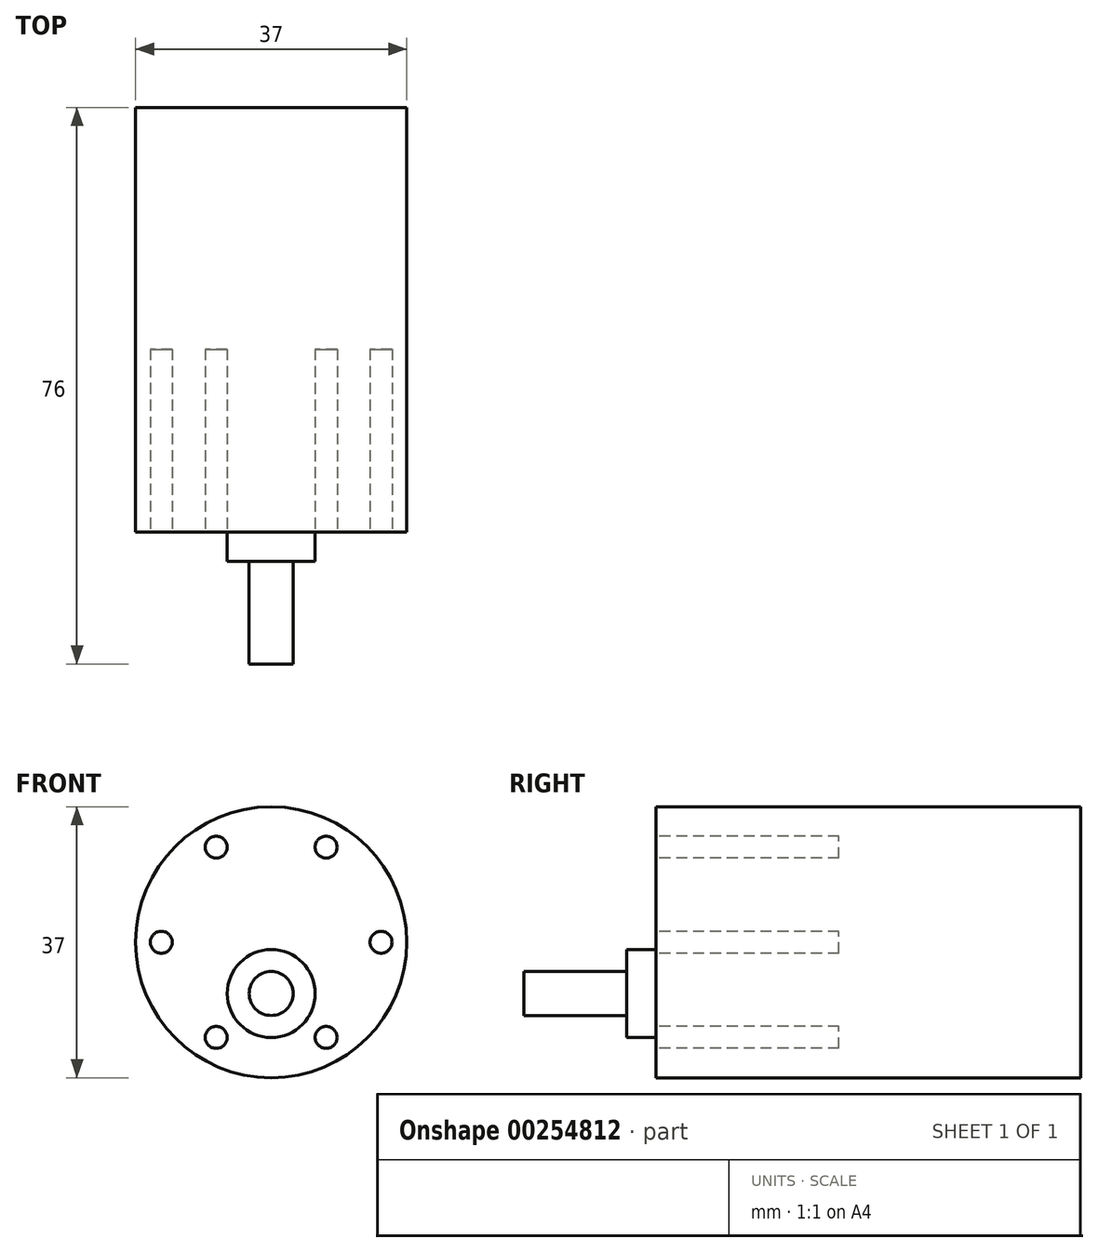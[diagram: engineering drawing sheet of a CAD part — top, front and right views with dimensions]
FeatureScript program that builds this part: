
annotation { "Feature Type Name" : "Feature", "Feature Type Description" : "" }
export const myFeature = defineFeature(function(context is Context, id is Id, definition is map)
    precondition{}
    {
        {
            var Q0;
            Q0=qCreatedBy(makeId("Front.planeOp"),FACE);
            var sketch = newSketch(context, id + "F0", { "sketchPlane" : qUnion([Q0])});
            skCircle(sketch, "E0", {"center": v(0, 0) * mm, "radius": 18.5 * mm});
            skCircle(sketch, "E1", {"center": v(0, -7) * mm, "radius": 6 * mm});
            skCircle(sketch, "E2", {"center": v(0, -7) * mm, "radius": 3 * mm});
            skCircle(sketch, "E3", {"center": v(-15, 0) * mm, "radius": 1.5 * mm});
            skCircle(sketch, "E4.1.0", {"center": v(-7.5, -13) * mm, "radius": 1.5 * mm});
            skCircle(sketch, "E4.2.0", {"center": v(7.5, -13) * mm, "radius": 1.5 * mm});
            skCircle(sketch, "E4.3.0", {"center": v(15, 0) * mm, "radius": 1.5 * mm});
            skCircle(sketch, "E4.4.0", {"center": v(7.5, 13) * mm, "radius": 1.5 * mm});
            skCircle(sketch, "E4.5.0", {"center": v(-7.5, 13) * mm, "radius": 1.5 * mm});
            skSolve(sketch);
        }
        {
            var Q0;
            Q0 = qSketchRegion(id + "F0", true);
            var Q1;
            Q1=makeQuery(id+"F0.imprint","IMPRINT",FACE,{"disambiguationData":[TD([[makeQuery(id+"F0.imprint","IMPRINT",EDGE,{"derivedFrom":sQuery(id+"F0.wireOp",EDGE,"E1")}),1.0]])]});
            var Q2;
            Q2=makeQuery(id+"F0.imprint","IMPRINT",FACE,{"disambiguationData":[TD([[makeQuery(id+"F0.imprint","IMPRINT",EDGE,{"derivedFrom":sQuery(id+"F0.wireOp",EDGE,"E2")}),1.0]])]});
            var Q3;
            Q3=makeQuery(id+"F0.imprint","IMPRINT",FACE,{"disambiguationData":[TD([[makeQuery(id+"F0.imprint","IMPRINT",EDGE,{"derivedFrom":sQuery(id+"F0.wireOp",EDGE,"E4.5.0")}),1.0]])]});
            var Q4;
            Q4=makeQuery(id+"F0.imprint","IMPRINT",FACE,{"disambiguationData":[TD([[makeQuery(id+"F0.imprint","IMPRINT",EDGE,{"derivedFrom":sQuery(id+"F0.wireOp",EDGE,"E4.4.0")}),1.0]])]});
            var Q5;
            Q5=makeQuery(id+"F0.imprint","IMPRINT",FACE,{"disambiguationData":[TD([[makeQuery(id+"F0.imprint","IMPRINT",EDGE,{"derivedFrom":sQuery(id+"F0.wireOp",EDGE,"E4.3.0")}),1.0]])]});
            var Q6;
            Q6=makeQuery(id+"F0.imprint","IMPRINT",FACE,{"disambiguationData":[TD([[makeQuery(id+"F0.imprint","IMPRINT",EDGE,{"derivedFrom":sQuery(id+"F0.wireOp",EDGE,"E4.2.0")}),1.0]])]});
            var Q7;
            Q7=makeQuery(id+"F0.imprint","IMPRINT",FACE,{"disambiguationData":[TD([[makeQuery(id+"F0.imprint","IMPRINT",EDGE,{"derivedFrom":sQuery(id+"F0.wireOp",EDGE,"E4.1.0")}),1.0]])]});
            var Q8;
            Q8=makeQuery(id+"F0.imprint","IMPRINT",FACE,{"disambiguationData":[TD([[makeQuery(id+"F0.imprint","IMPRINT",EDGE,{"derivedFrom":sQuery(id+"F0.wireOp",EDGE,"E3")}),1.0]])]});
            extrude(context, id + "F1", {"entities" : qUnion([Q0, Q1, Q2, Q3, Q4, Q5, Q6, Q7, Q8]), "oppositeDirection" : true, "depth" : 58 * mm});
        }
        {
            var Q0;
            Q0=makeQuery(id+"F0.imprint","IMPRINT",FACE,{"disambiguationData":[TD([[makeQuery(id+"F0.imprint","IMPRINT",EDGE,{"derivedFrom":sQuery(id+"F0.wireOp",EDGE,"E1")}),1.0]])]});
            var Q1;
            Q1=makeQuery(id+"F0.imprint","IMPRINT",FACE,{"disambiguationData":[TD([[makeQuery(id+"F0.imprint","IMPRINT",EDGE,{"derivedFrom":sQuery(id+"F0.wireOp",EDGE,"E2")}),1.0]])]});
            extrude(context, id + "F2", {"entities" : qUnion([Q0, Q1]), "operationType" : NewBodyOperationType.ADD, "depth" : 4 * mm});
        }
        {
            var Q0;
            Q0=makeQuery(id+"F0.imprint","IMPRINT",FACE,{"disambiguationData":[TD([[makeQuery(id+"F0.imprint","IMPRINT",EDGE,{"derivedFrom":sQuery(id+"F0.wireOp",EDGE,"E2")}),1.0]])]});
            extrude(context, id + "F3", {"entities" : qUnion([Q0]), "operationType" : NewBodyOperationType.ADD, "depth" : 18 * mm});
        }
        {
            var Q0;
            Q0=makeQuery(id+"F0.imprint","IMPRINT",FACE,{"disambiguationData":[TD([[makeQuery(id+"F0.imprint","IMPRINT",EDGE,{"derivedFrom":sQuery(id+"F0.wireOp",EDGE,"E4.4.0")}),1.0]])]});
            var Q1;
            Q1=makeQuery(id+"F0.imprint","IMPRINT",FACE,{"disambiguationData":[TD([[makeQuery(id+"F0.imprint","IMPRINT",EDGE,{"derivedFrom":sQuery(id+"F0.wireOp",EDGE,"E4.5.0")}),1.0]])]});
            var Q2;
            Q2=makeQuery(id+"F0.imprint","IMPRINT",FACE,{"disambiguationData":[TD([[makeQuery(id+"F0.imprint","IMPRINT",EDGE,{"derivedFrom":sQuery(id+"F0.wireOp",EDGE,"E3")}),1.0]])]});
            var Q3;
            Q3=makeQuery(id+"F0.imprint","IMPRINT",FACE,{"disambiguationData":[TD([[makeQuery(id+"F0.imprint","IMPRINT",EDGE,{"derivedFrom":sQuery(id+"F0.wireOp",EDGE,"E4.2.0")}),1.0]])]});
            var Q4;
            Q4=makeQuery(id+"F0.imprint","IMPRINT",FACE,{"disambiguationData":[TD([[makeQuery(id+"F0.imprint","IMPRINT",EDGE,{"derivedFrom":sQuery(id+"F0.wireOp",EDGE,"E4.3.0")}),1.0]])]});
            var Q5;
            Q5=makeQuery(id+"F0.imprint","IMPRINT",FACE,{"disambiguationData":[TD([[makeQuery(id+"F0.imprint","IMPRINT",EDGE,{"derivedFrom":sQuery(id+"F0.wireOp",EDGE,"E4.1.0")}),1.0]])]});
            extrude(context, id + "F4", {"entities" : qUnion([Q0, Q1, Q2, Q3, Q4, Q5]), "operationType" : NewBodyOperationType.REMOVE, "oppositeDirection" : true, "depth" : 25 * mm});
        }
    });
